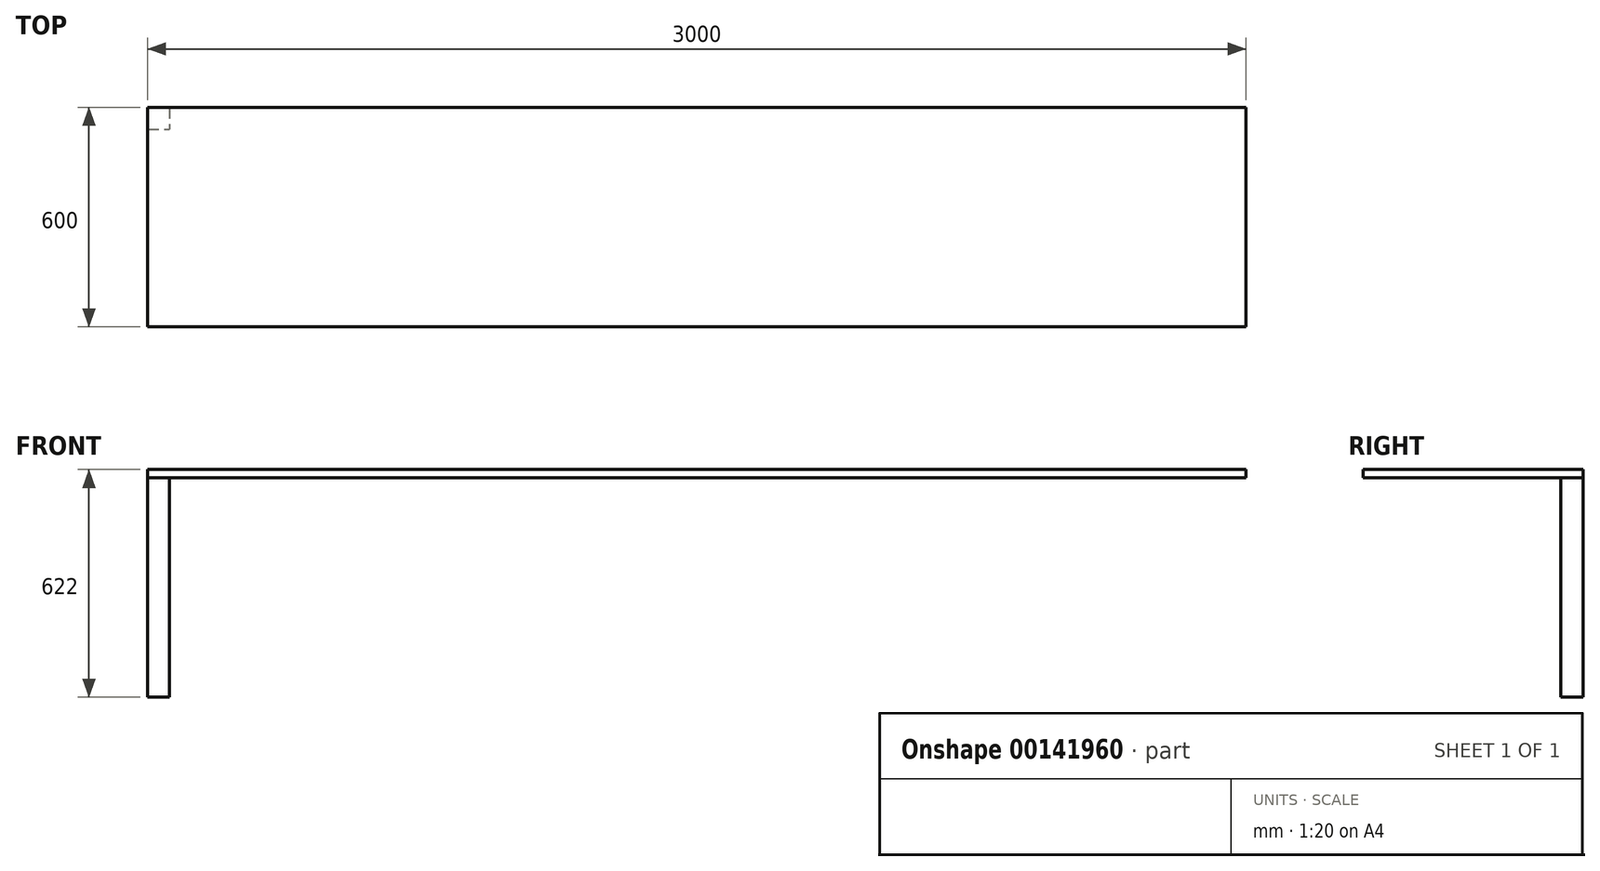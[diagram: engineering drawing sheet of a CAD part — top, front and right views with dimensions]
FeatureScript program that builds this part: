
annotation { "Feature Type Name" : "Feature", "Feature Type Description" : "" }
export const myFeature = defineFeature(function(context is Context, id is Id, definition is map)
    precondition{}
    {
        {
            var Q0;
            Q0=qCreatedBy(makeId("Top.planeOp"),FACE);
            var sketch = newSketch(context, id + "F0", { "sketchPlane" : qUnion([Q0])});
            skLineSegment(sketch, "E0.bottom", {"start": v(-118.62, -27.9) * mm, "end": v(2881.38, -27.9) * mm});
            skLineSegment(sketch, "E0.top", {"start": v(-118.62, 572.1) * mm, "end": v(2881.38, 572.1) * mm});
            skLineSegment(sketch, "E0.left", {"start": v(-118.62, -27.9) * mm, "end": v(-118.62, 572.1) * mm});
            skLineSegment(sketch, "E0.right", {"start": v(2881.38, -27.9) * mm, "end": v(2881.38, 572.1) * mm});
            skSolve(sketch);
        }
        {
            var Q0;
            Q0 = qSketchRegion(id + "F0", true);
            var Q1;
            Q1=makeQuery(id+"F0.imprint","IMPRINT",FACE,{"disambiguationData":[TD([[makeQuery(id+"F0.imprint","IMPRINT",EDGE,{"derivedFrom":sQuery(id+"F0.wireOp",EDGE,"E0.bottom")}),1.0]])]});
            extrude(context, id + "F1", {"entities" : qUnion([Q0, Q1]), "depth" : 22 * mm});
        }
        {
            var Q0;
            Q0=makeQuery(id+"F1.opExtrude","CAP_FACE",FACE,{"disambiguationData":[OSD([sQuery(id+"F0.wireOp",EDGE,"E0.bottom"),sQuery(id+"F0.wireOp",EDGE,"E0.top"),sQuery(id+"F0.wireOp",EDGE,"E0.left"),sQuery(id+"F0.wireOp",EDGE,"E0.right")])],"isStart":true});
            var sketch = newSketch(context, id + "F2", { "sketchPlane" : qUnion([Q0])});
            skLineSegment(sketch, "E1.bottom", {"start": v(-118.62, 27.9) * mm, "end": v(-58.62, 27.9) * mm});
            skLineSegment(sketch, "E1.top", {"start": v(-118.62, -32.1) * mm, "end": v(-58.62, -32.1) * mm});
            skLineSegment(sketch, "E1.left", {"start": v(-118.62, 27.9) * mm, "end": v(-118.62, -32.1) * mm});
            skLineSegment(sketch, "E1.right", {"start": v(-58.62, 27.9) * mm, "end": v(-58.62, -32.1) * mm});
            skLineSegment(sketch, "E2.bottom", {"start": v(-118.62, -572.1) * mm, "end": v(-58.62, -572.1) * mm});
            skLineSegment(sketch, "E2.top", {"start": v(-118.62, -512.1) * mm, "end": v(-58.62, -512.1) * mm});
            skLineSegment(sketch, "E2.left", {"start": v(-118.62, -572.1) * mm, "end": v(-118.62, -512.1) * mm});
            skLineSegment(sketch, "E2.right", {"start": v(-58.62, -572.1) * mm, "end": v(-58.62, -512.1) * mm});
            skLineSegment(sketch, "E3.bottom", {"start": v(2881.38, -572.1) * mm, "end": v(2821.38, -572.1) * mm});
            skLineSegment(sketch, "E3.top", {"start": v(2881.38, -512.1) * mm, "end": v(2821.38, -512.1) * mm});
            skLineSegment(sketch, "E3.left", {"start": v(2881.38, -572.1) * mm, "end": v(2881.38, -512.1) * mm});
            skLineSegment(sketch, "E3.right", {"start": v(2821.38, -572.1) * mm, "end": v(2821.38, -512.1) * mm});
            skLineSegment(sketch, "E4.bottom", {"start": v(2881.38, 27.9) * mm, "end": v(2821.38, 27.9) * mm});
            skLineSegment(sketch, "E4.top", {"start": v(2881.38, -32.1) * mm, "end": v(2821.38, -32.1) * mm});
            skLineSegment(sketch, "E4.left", {"start": v(2881.38, 27.9) * mm, "end": v(2881.38, -32.1) * mm});
            skLineSegment(sketch, "E4.right", {"start": v(2821.38, 27.9) * mm, "end": v(2821.38, -32.1) * mm});
            skSolve(sketch);
        }
        {
            var Q0;
            Q0=makeQuery(id+"F2.imprint","IMPRINT",FACE,{"disambiguationData":[TD([[makeQuery(id+"F2.imprint","IMPRINT",EDGE,{"derivedFrom":sQuery(id+"F2.wireOp",EDGE,"E2.bottom")}),1.0]])]});
            extrude(context, id + "F3", {"entities" : qUnion([Q0]), "operationType" : NewBodyOperationType.ADD, "depth" : 600 * mm});
        }
    });
